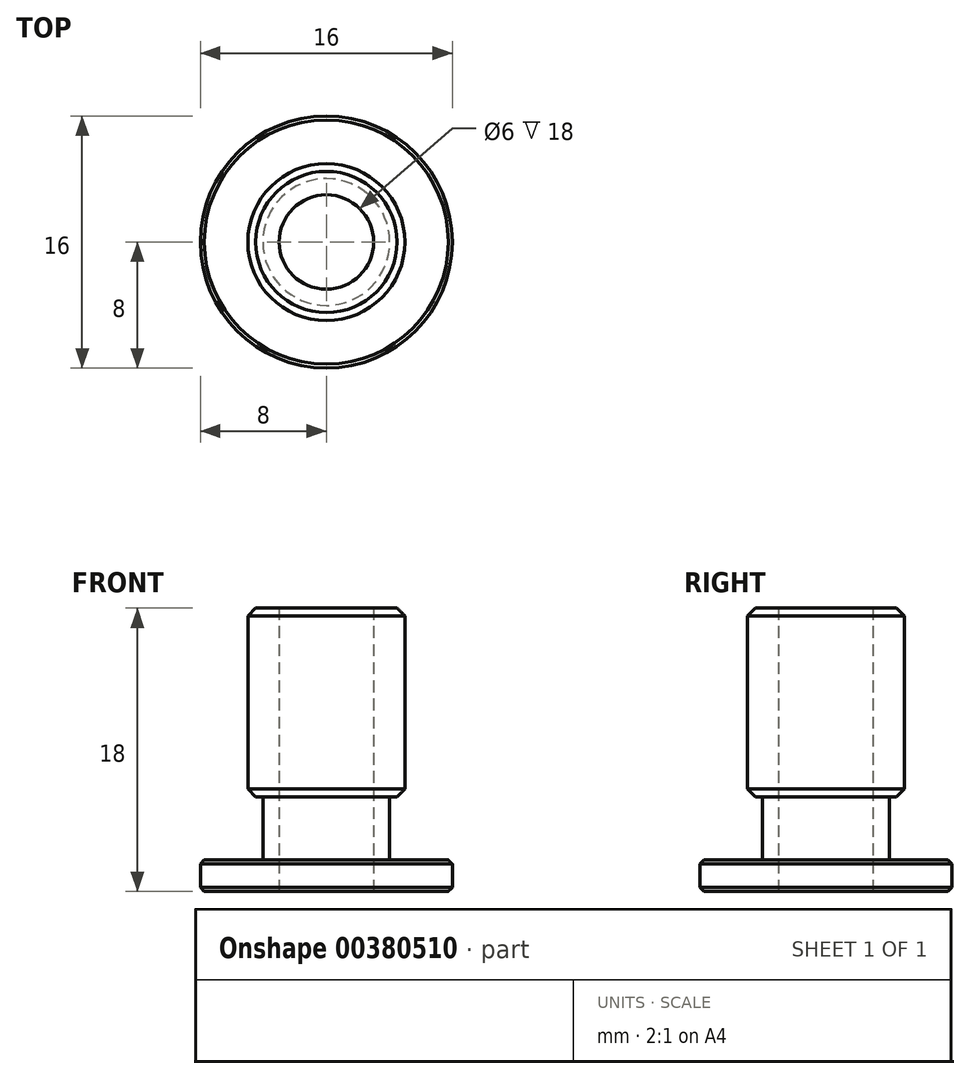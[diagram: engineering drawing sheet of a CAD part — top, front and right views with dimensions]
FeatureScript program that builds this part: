
annotation { "Feature Type Name" : "Feature", "Feature Type Description" : "" }
export const myFeature = defineFeature(function(context is Context, id is Id, definition is map)
    precondition{}
    {
        {
            var Q0;
            Q0=qCreatedBy(makeId("Top.planeOp"),FACE);
            var sketch = newSketch(context, id + "F0", { "sketchPlane" : qUnion([Q0])});
            skCircle(sketch, "E0", {"center": v(0, 0) * mm, "radius": 8 * mm});
            skCircle(sketch, "E1", {"center": v(0, 0) * mm, "radius": 4.99 * mm});
            skCircle(sketch, "E2", {"center": v(0, 0) * mm, "radius": 3 * mm});
            skCircle(sketch, "E3", {"center": v(0, 0) * mm, "radius": 4.03 * mm});
            skSolve(sketch);
        }
        {
            var Q0;
            Q0=makeQuery(id+"F0.imprint","IMPRINT",FACE,{"disambiguationData":[TD([[makeQuery(id+"F0.imprint","IMPRINT",EDGE,{"derivedFrom":sQuery(id+"F0.wireOp",EDGE,"E0")}),1.0]])]});
            var Q1;
            Q1=makeQuery(id+"F0.imprint","IMPRINT",FACE,{"disambiguationData":[TD([[makeQuery(id+"F0.imprint","IMPRINT",EDGE,{"derivedFrom":sQuery(id+"F0.wireOp",EDGE,"E1")}),1.0]])]});
            extrude(context, id + "F1", {"entities" : qUnion([Q0, Q1]), "depth" : 2 * mm});
        }
        {
            var Q0;
            Q0=makeQuery(id+"F0.imprint","IMPRINT",FACE,{"disambiguationData":[TD([[makeQuery(id+"F0.imprint","IMPRINT",EDGE,{"derivedFrom":sQuery(id+"F0.wireOp",EDGE,"E2")}),1.0]])]});
            var Q1;
            Q1=makeQuery(id+"F0.imprint","IMPRINT",FACE,{"disambiguationData":[TD([[makeQuery(id+"F0.imprint","IMPRINT",EDGE,{"derivedFrom":sQuery(id+"F0.wireOp",EDGE,"E2")}),-1.0]])]});
            extrude(context, id + "F2", {"entities" : qUnion([Q0, Q1]), "operationType" : NewBodyOperationType.ADD, "depth" : 18 * mm});
        }
        {
            var Q0;
            Q0=makeQuery(id+"F2.opExtrude","CAP_FACE",FACE,{"disambiguationData":[OSD([sQuery(id+"F0.wireOp",EDGE,"E3")])],"isStart":false});
            var sketch = newSketch(context, id + "F3", { "sketchPlane" : qUnion([Q0])});
            skCircle(sketch, "E4.0", {"center": v(0, 0) * mm, "radius": 4.99 * mm});
            skSolve(sketch);
        }
        {
            var Q0;
            Q0=makeQuery(id+"F3.imprint","IMPRINT",FACE,{"disambiguationData":[TD([[makeQuery(id+"F3.imprint","IMPRINT",EDGE,{"derivedFrom":sQuery(id+"F3.wireOp",EDGE,"E4.0")}),1.0]])]});
            extrude(context, id + "F4", {"entities" : qUnion([Q0]), "operationType" : NewBodyOperationType.ADD, "oppositeDirection" : true, "depth" : 12 * mm});
        }
        {
            var Q0;
            Q0=makeQuery(id+"F0.imprint","IMPRINT",FACE,{"disambiguationData":[TD([[makeQuery(id+"F0.imprint","IMPRINT",EDGE,{"derivedFrom":sQuery(id+"F0.wireOp",EDGE,"E2")}),1.0]])]});
            extrude(context, id + "F5", {"entities" : qUnion([Q0]), "operationType" : NewBodyOperationType.REMOVE, "depth" : 44.1 * mm});
        }
        {
            var Q0;
            Q0=makeQuery(id+"F1.opExtrude","SWEPT_FACE",FACE,{"disambiguationData":[OSD([sQuery(id+"F0.wireOp",EDGE,"E0")])]});
            chamfer(context, id + "F6", {"entities" : qUnion([Q0]), "width" : .25 * mm, "tangentPropagation" : true});
        }
        {
            var Q0;
            Q0=makeQuery(id+"F4.opExtrude","CAP_EDGE",EDGE,{"disambiguationData":[OSD([sQuery(id+"F3.wireOp",EDGE,"E4.0")])],"isStart":false});
            var Q1;
            Q1=makeQuery(id+"F4.opExtrude","CAP_EDGE",EDGE,{"disambiguationData":[OSD([sQuery(id+"F3.wireOp",EDGE,"E4.0")])],"isStart":true});
            chamfer(context, id + "F7", {"entities" : qUnion([Q0, Q1]), "width" : .5 * mm, "tangentPropagation" : true});
        }
    });
